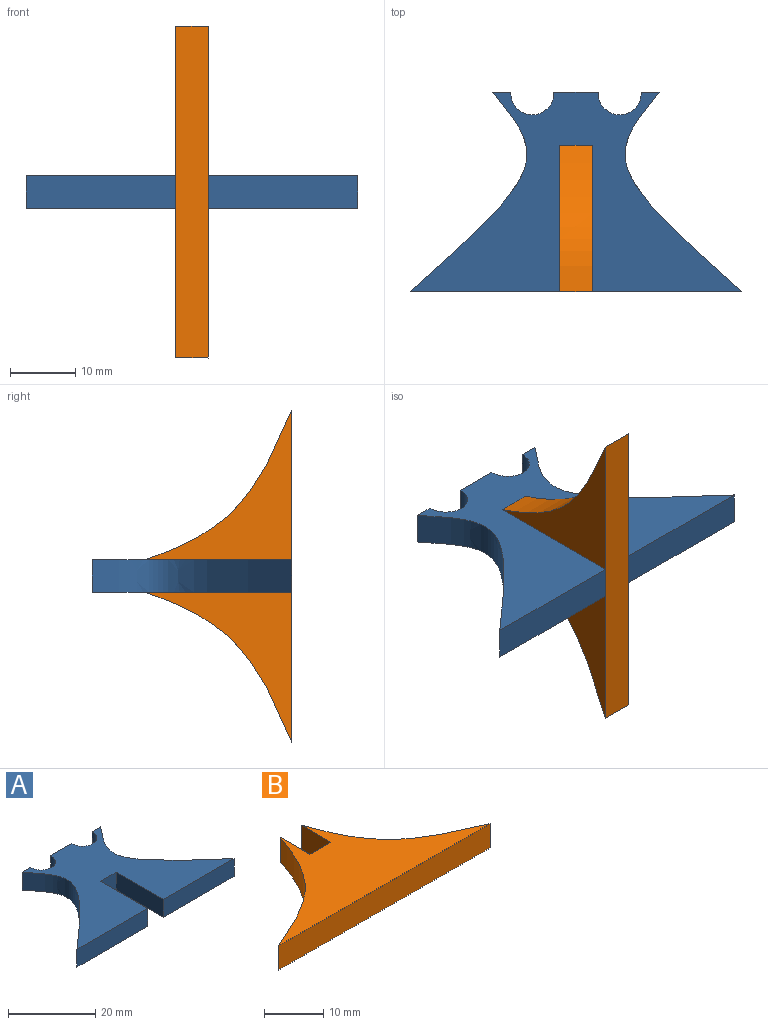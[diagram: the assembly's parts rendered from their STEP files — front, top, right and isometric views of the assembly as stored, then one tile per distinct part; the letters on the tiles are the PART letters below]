
ASSEMBLY  parts=2 mates=1
PART A: 14 faces, bbox 50.8x30.5x5 mm
  f0: plane 5x2.73mm, normal (0,1,0), area 13.6mm2, adj f1,f11,f12,f13
  f1: cylinder r=3.29mm len=6.58mm, axis (0,0,-1), area 53.3mm2, adj f0,f2,f12,f13
  f2: plane 6.81x5mm, normal (0,1,0), area 34mm2, adj f1,f3,f12,f13
  f3: cylinder r=3.29mm len=6.58mm, axis (0,0,-1), area 53.3mm2, adj f2,f4,f12,f13
  f4: plane 5x2.73mm, normal (0,1,0), area 13.6mm2, adj f3,f5,f12,f13
  f5: extruded ~30.48x17.88mm, area 195.8mm2, adj f4,f6,f12,f13
  f6: plane 22.9x5mm, normal (0,-1,0), area 114.5mm2, adj f5,f7,f12,f13
  f7: plane 15.24x5mm, normal (1,0,0), area 76.2mm2, adj f6,f8,f12,f13
  f8: plane 5x5mm, normal (0,-1,0), area 25mm2, adj f7,f9,f12,f13
  f9: plane 15.24x5mm, normal (-1,0,0), area 76.2mm2, adj f8,f10,f12,f13
  f10: plane 22.9x5mm, normal (0,-1,0), area 114.5mm2, adj f9,f11,f12,f13
  f11: extruded ~30.48x17.88mm, area 195.8mm2, adj f0,f10,f12,f13
  f12: plane 50.8x30.48mm, normal (0,0,1), area 684.9mm2, adj f0,f1,f2,f3,f4,f5,f6,f7
  f13: plane 50.8x30.48mm, normal (0,0,-1), area 684.9mm2, adj f0,f1,f2,f3,f4,f5,f6,f7
PART B: 8 faces, bbox 50.8x22.4x5 mm
  f0: plane 50.8x5mm, normal (0,-1,0), area 254mm2, adj f1,f5,f6,f7
  f1: extruded ~22.9x22.38mm, area 167.4mm2, adj f0,f2,f6,f7
  f2: plane 7.14x5mm, normal (-1,0,0), area 35.7mm2, adj f1,f3,f6,f7
  f3: plane 5x5mm, normal (0,1,0), area 25mm2, adj f2,f4,f6,f7
  f4: plane 7.14x5mm, normal (1,0,0), area 35.7mm2, adj f3,f5,f6,f7
  f5: extruded ~22.9x22.38mm, area 167.4mm2, adj f0,f4,f6,f7
  f6: plane 50.8x22.38mm, normal (0,0,1), area 409.2mm2, adj f0,f1,f2,f3,f4,f5
  f7: plane 50.8x22.38mm, normal (0,0,-1), area 409.2mm2, adj f0,f1,f2,f3,f4,f5
PLACE A t=(-0.49,-14.59,-3.14)mm
PLACE B rot(axis=(0,1,0),90deg) t=(-2.99,-14.58,63.84)mm
MATE slider B.f3 <-> A.f8  axis (0,1,0) through (-0.49,0.66,-0.64)mm
